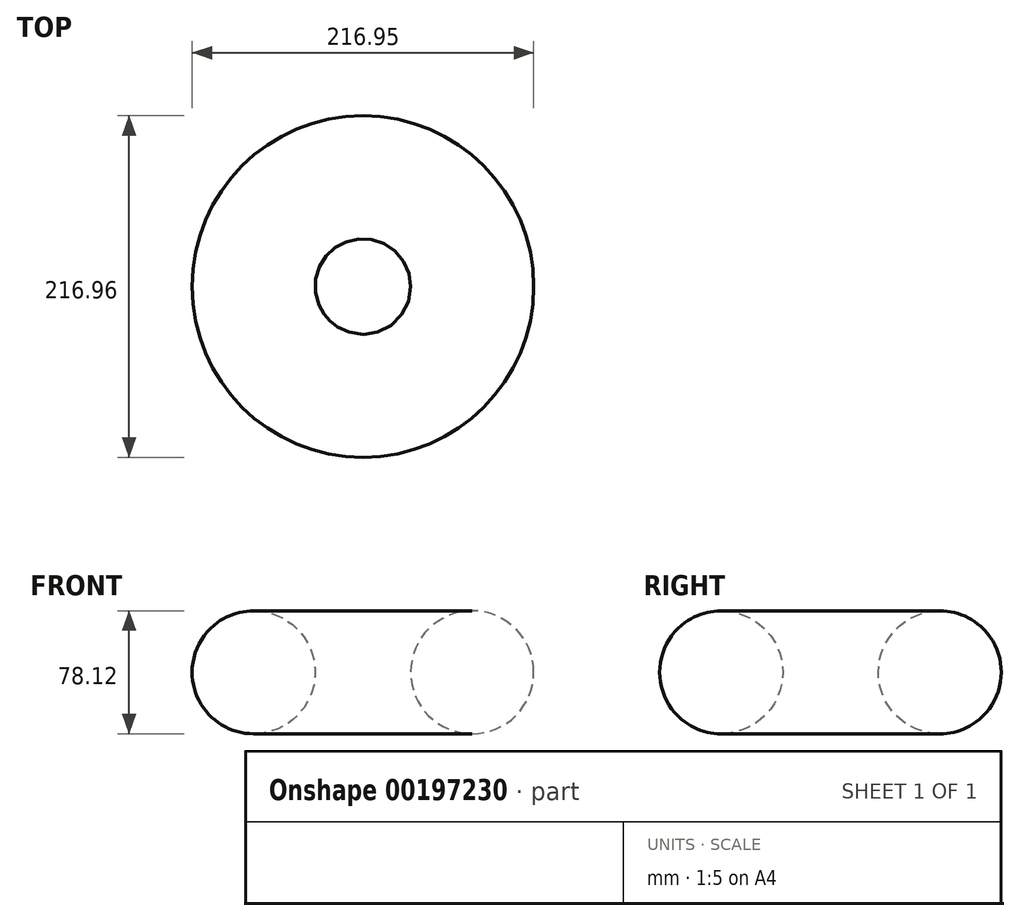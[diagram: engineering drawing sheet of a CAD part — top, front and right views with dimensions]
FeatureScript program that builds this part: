
annotation { "Feature Type Name" : "Feature", "Feature Type Description" : "" }
export const myFeature = defineFeature(function(context is Context, id is Id, definition is map)
    precondition{}
    {
        {
            var Q0;
            Q0=qCreatedBy(makeId("Front.planeOp"),FACE);
            var sketch = newSketch(context, id + "F0", { "sketchPlane" : qUnion([Q0])});
            skCircle(sketch, "E0", {"center": v(0, 0) * mm, "radius": 39.06 * mm});
            skLineSegment(sketch, "E1", {"start": v(-69.42, 39.06) * mm, "end": v(-69.42, -38.24) * mm});
            skPoint(sketch, "E2.start.orphan", {"position": v(0, 39.06) * mm});
            skSolve(sketch);
        }
        {
            var Q0;
            Q0=makeQuery(id+"F0.imprint","IMPRINT",FACE,{"disambiguationData":[TD([[makeQuery(id+"F0.imprint","IMPRINT",EDGE,{"derivedFrom":sQuery(id+"F0.wireOp",EDGE,"E0")}),1.0]])]});
            var Q1;
            Q1=sQuery(id+"F0.wireOp",EDGE,"E1");
            revolve(context, id + "F1", {"entities" : qUnion([Q0]), "axis" : qUnion([Q1]), "revolveType" : RevolveType.FULL});
        }
    });
